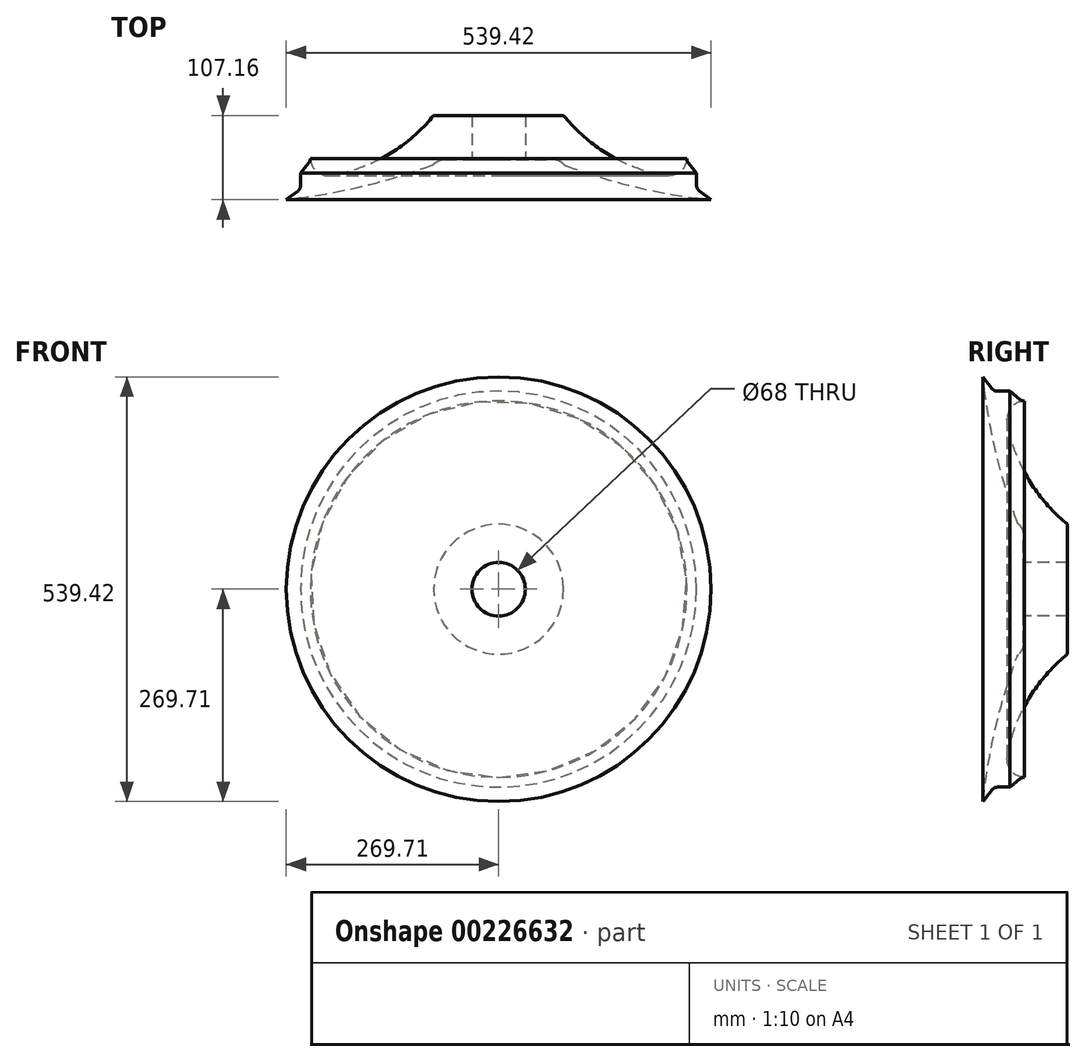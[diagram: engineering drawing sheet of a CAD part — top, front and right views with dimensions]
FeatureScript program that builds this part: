
annotation { "Feature Type Name" : "Feature", "Feature Type Description" : "" }
export const myFeature = defineFeature(function(context is Context, id is Id, definition is map)
    precondition{}
    {
        {
            var Q0;
            Q0=qCreatedBy(makeId("Right.planeOp"),FACE);
            var sketch = newSketch(context, id + "F0", { "sketchPlane" : qUnion([Q0])});
            skLineSegment(sketch, "E0", {"start": v(-123.86, 254) * mm, "end": v(-109.52, 254) * mm, "construction": true});
            skLineSegment(sketch, "E1", {"start": v(0, 0) * mm, "end": v(0, 254) * mm, "construction": true});
            skPoint(sketch, "E1.endSnap0", {"position": v(0, 254) * mm});
            skLineSegment(sketch, "E2", {"start": v(-140.14, 271.25) * mm, "end": v(-128.9, 256.5) * mm});
            skLineSegment(sketch, "E3", {"start": v(-105.46, 252.53) * mm, "end": v(-94.14, 243.13) * mm});
            skLineSegment(sketch, "E4", {"start": v(-89.81, 241.67) * mm, "end": v(77.91, 248.76) * mm});
            skLineSegment(sketch, "E5", {"start": v(79.7, 249.1) * mm, "end": v(93.05, 253.66) * mm});
            skLineSegment(sketch, "E6", {"start": v(95.1, 254) * mm, "end": v(123.47, 254) * mm});
            skLineSegment(sketch, "E7", {"start": v(128.86, 257) * mm, "end": v(138.45, 272.41) * mm});
            skPoint(sketch, "E8.visualSharp", {"position": v(-127, 254) * mm});
            skArc(sketch, "E8.filletArc", {"start": v(-128.9, 256.5) * mm, "mid": v(-126.67, 254.66) * mm, "end": v(-123.86, 254) * mm});
            skPoint(sketch, "E9.newPointA", {"position": v(127, 254) * mm});
            skArc(sketch, "E9.filletArc", {"start": v(-105.46, 252.53) * mm, "mid": v(-107.36, 253.62) * mm, "end": v(-109.52, 254) * mm});
            skPoint(sketch, "E10.visualSharp", {"position": v(-92.26, 241.57) * mm});
            skArc(sketch, "E10.filletArc", {"start": v(-94.14, 243.13) * mm, "mid": v(-92.11, 242) * mm, "end": v(-89.81, 241.67) * mm});
            skPoint(sketch, "E11.visualSharp", {"position": v(78.83, 248.8) * mm});
            skArc(sketch, "E11.filletArc", {"start": v(77.91, 248.76) * mm, "mid": v(78.82, 248.86) * mm, "end": v(79.7, 249.1) * mm});
            skPoint(sketch, "E12.visualSharp", {"position": v(94.04, 254) * mm});
            skArc(sketch, "E12.filletArc", {"start": v(95.1, 254) * mm, "mid": v(94.06, 253.91) * mm, "end": v(93.05, 253.66) * mm});
            skArc(sketch, "E13.filletArc", {"start": v(123.47, 254) * mm, "mid": v(126.56, 254.8) * mm, "end": v(128.86, 257) * mm});
            skSolve(sketch);
        }
        {
            var Q0;
            Q0=qCreatedBy(makeId("Right.planeOp"),FACE);
            var sketch = newSketch(context, id + "F1", { "sketchPlane" : qUnion([Q0])});
            skLineSegment(sketch, "E14.0", {"start": v(131.02, 255.65) * mm, "end": v(140.61, 271.07) * mm});
            skLineSegment(sketch, "E14.1", {"start": v(-108.14, 251.46) * mm, "end": v(-95.76, 241.18) * mm});
            skLineSegment(sketch, "E14.2", {"start": v(-123.86, 251.46) * mm, "end": v(-108.14, 251.46) * mm});
            skArc(sketch, "E14.3", {"start": v(-130.93, 254.96) * mm, "mid": v(-127.8, 252.38) * mm, "end": v(-123.86, 251.46) * mm});
            skLineSegment(sketch, "E14.4", {"start": v(-142.16, 269.7) * mm, "end": v(-130.93, 254.96) * mm});
            skArc(sketch, "E14.5", {"start": v(-95.76, 241.18) * mm, "mid": v(-92.93, 239.6) * mm, "end": v(-89.7, 239.13) * mm});
            skLineSegment(sketch, "E14.6", {"start": v(-89.7, 239.13) * mm, "end": v(78.02, 246.22) * mm});
            skArc(sketch, "E14.7", {"start": v(78.02, 246.22) * mm, "mid": v(79.29, 246.37) * mm, "end": v(80.52, 246.7) * mm});
            skLineSegment(sketch, "E14.8", {"start": v(80.52, 246.7) * mm, "end": v(94.47, 251.46) * mm});
            skLineSegment(sketch, "E14.9", {"start": v(94.47, 251.46) * mm, "end": v(123.47, 251.46) * mm});
            skArc(sketch, "E14.10", {"start": v(123.47, 251.46) * mm, "mid": v(127.79, 252.58) * mm, "end": v(131.02, 255.65) * mm});
            skLineSegment(sketch, "E15.0", {"start": v(-105.46, 252.53) * mm, "end": v(-94.14, 243.13) * mm});
            skLineSegment(sketch, "E15.1", {"start": v(-140.14, 271.25) * mm, "end": v(-128.9, 256.5) * mm});
            skArc(sketch, "E15.2", {"start": v(-128.9, 256.5) * mm, "mid": v(-126.67, 254.66) * mm, "end": v(-123.86, 254) * mm});
            skLineSegment(sketch, "E15.3", {"start": v(-123.86, 254) * mm, "end": v(-109.52, 254) * mm});
            skArc(sketch, "E15.4", {"start": v(-105.46, 252.53) * mm, "mid": v(-107.36, 253.62) * mm, "end": v(-109.52, 254) * mm});
            skPoint(sketch, "E15.5", {"position": v(-92.26, 241.57) * mm});
            skArc(sketch, "E15.6", {"start": v(-94.14, 243.13) * mm, "mid": v(-92.11, 242) * mm, "end": v(-89.81, 241.67) * mm});
            skLineSegment(sketch, "E15.7", {"start": v(-89.81, 241.67) * mm, "end": v(77.91, 248.76) * mm});
            skLineSegment(sketch, "E15.8", {"start": v(128.86, 257) * mm, "end": v(138.45, 272.41) * mm});
            skArc(sketch, "E15.9", {"start": v(123.47, 254) * mm, "mid": v(126.56, 254.8) * mm, "end": v(128.86, 257) * mm});
            skLineSegment(sketch, "E15.10", {"start": v(95.1, 254) * mm, "end": v(123.47, 254) * mm});
            skArc(sketch, "E15.11", {"start": v(95.1, 254) * mm, "mid": v(94.06, 253.91) * mm, "end": v(93.05, 253.66) * mm});
            skLineSegment(sketch, "E15.12", {"start": v(79.7, 249.1) * mm, "end": v(93.05, 253.66) * mm});
            skArc(sketch, "E15.13", {"start": v(77.91, 248.76) * mm, "mid": v(78.82, 248.86) * mm, "end": v(79.7, 249.1) * mm});
            skLineSegment(sketch, "E16", {"start": v(-140.14, 271.25) * mm, "end": v(-142.16, 269.7) * mm});
            skLineSegment(sketch, "E17", {"start": v(138.45, 272.41) * mm, "end": v(140.61, 271.07) * mm});
            skLineSegment(sketch, "E18", {"start": v(0, 0) * mm, "end": v(-132.17, 0) * mm, "construction": true});
            skSolve(sketch);
        }
        {
            var Q0;
            Q0=qCreatedBy(makeId("Right.planeOp"),FACE);
            var sketch = newSketch(context, id + "F2", { "sketchPlane" : qUnion([Q0])});
            skLineSegment(sketch, "E19", {"start": v(-35, 0) * mm, "end": v(-35, 116.08) * mm, "construction": true});
            skLineSegment(sketch, "E20", {"start": v(0, 34) * mm, "end": v(-35, 34) * mm, "construction": true});
            skLineSegment(sketch, "E21", {"start": v(0, 57.15) * mm, "end": v(-35, 57.15) * mm, "construction": true});
            skLineSegment(sketch, "E22", {"start": v(-35, 34) * mm, "end": v(-90.96, 34) * mm});
            skLineSegment(sketch, "E23", {"start": v(-35, 34) * mm, "end": v(-35, 82.55) * mm});
            skArc(sketch, "E24", {"start": v(-111.34, 212.33) * mm, "mid": v(-85.02, 140.47) * mm, "end": v(-35, 82.55) * mm});
            skArc(sketch, "E25", {"start": v(-89.7, 239.13) * mm, "mid": v(-106.58, 230.62) * mm, "end": v(-111.34, 212.33) * mm});
            skArc(sketch, "E26.0", {"start": v(-95.76, 241.18) * mm, "mid": v(-92.93, 239.6) * mm, "end": v(-89.7, 239.13) * mm});
            skLineSegment(sketch, "E26.1", {"start": v(-123.86, 251.46) * mm, "end": v(-108.14, 251.46) * mm});
            skLineSegment(sketch, "E26.2", {"start": v(-108.14, 251.46) * mm, "end": v(-95.76, 241.18) * mm});
            skArc(sketch, "E26.3", {"start": v(-130.93, 254.96) * mm, "mid": v(-127.8, 252.38) * mm, "end": v(-123.86, 251.46) * mm});
            skLineSegment(sketch, "E26.4", {"start": v(-142.16, 269.7) * mm, "end": v(-130.93, 254.96) * mm});
            skLineSegment(sketch, "E27", {"start": v(-90.96, 34) * mm, "end": v(-90.96, 68.2) * mm});
            skArc(sketch, "E28", {"start": v(-90.96, 68.2) * mm, "mid": v(-92.63, 76.26) * mm, "end": v(-97.37, 83) * mm});
            skArc(sketch, "E29", {"start": v(-142.16, 269.7) * mm, "mid": v(-126.3, 176.22) * mm, "end": v(-98.98, 85.42) * mm});
            skPoint(sketch, "E30.visualSharp", {"position": v(-98.42, 83.91) * mm});
            skArc(sketch, "E30.filletArc", {"start": v(-98.98, 85.42) * mm, "mid": v(-98.32, 84.11) * mm, "end": v(-97.37, 83) * mm});
            skLineSegment(sketch, "E31", {"start": v(-132.89, 0) * mm, "end": v(0, 0) * mm, "construction": true});
            skSolve(sketch);
        }
        {
            var Q0;
            Q0=qSketchRegion(id+"F2",true);
            var Q1;
            Q1=sQuery(id+"F2.wireOp",EDGE,"E31");
            revolve(context, id + "F3", {"entities" : qUnion([Q0]), "axis" : qUnion([Q1]), "revolveType" : RevolveType.FULL});
        }
    });
